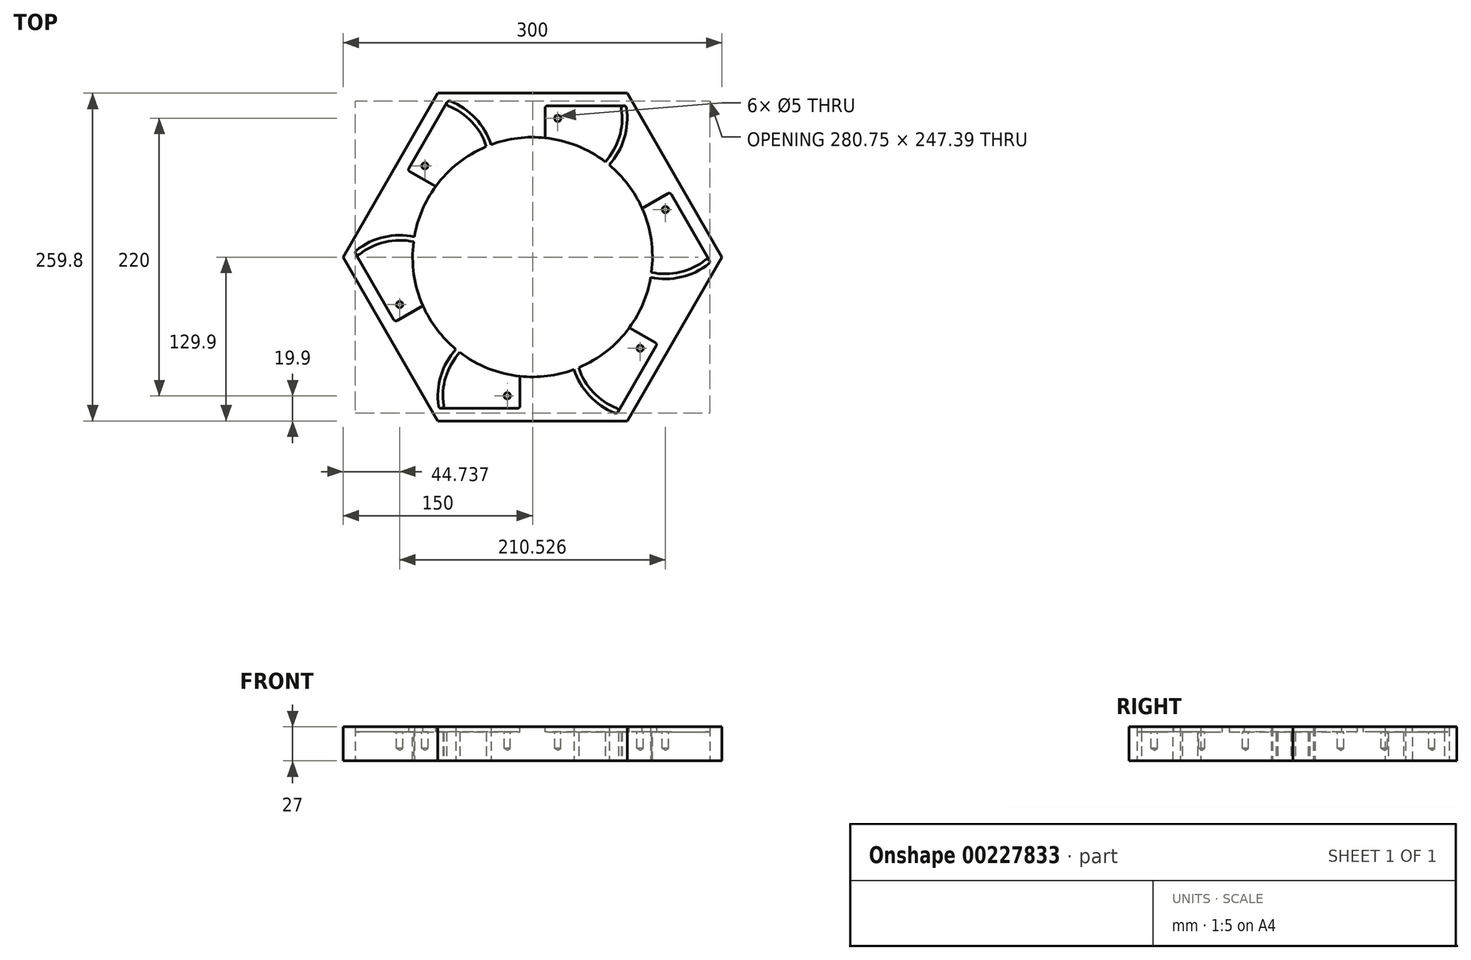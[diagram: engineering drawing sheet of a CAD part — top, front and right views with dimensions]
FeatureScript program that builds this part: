
annotation { "Feature Type Name" : "Feature", "Feature Type Description" : "" }
export const myFeature = defineFeature(function(context is Context, id is Id, definition is map)
    precondition{}
    {
        {
            var Q0;
            Q0=qCreatedBy(makeId("Top.planeOp"),FACE);
            var sketch = newSketch(context, id + "F0", { "sketchPlane" : qUnion([Q0])});
            skCircle(sketch, "E0.cCircle", {"center": v(0, 0) * mm, "radius": 150 * mm, "construction": true});
            skLineSegment(sketch, "E0.0", {"start": v(-75, 129.9) * mm, "end": v(75, 129.9) * mm});
            skLineSegment(sketch, "E0.1", {"start": v(75, 129.9) * mm, "end": v(150, 0) * mm});
            skLineSegment(sketch, "E0.2", {"start": v(150, 0) * mm, "end": v(75, -129.9) * mm});
            skLineSegment(sketch, "E0.3", {"start": v(75, -129.9) * mm, "end": v(-75, -129.9) * mm});
            skLineSegment(sketch, "E0.4", {"start": v(-75, -129.9) * mm, "end": v(-150, 0) * mm});
            skLineSegment(sketch, "E0.5", {"start": v(-150, 0) * mm, "end": v(-75, 129.9) * mm});
            skCircle(sketch, "E1", {"center": v(0, 0) * mm, "radius": 95 * mm});
            skSolve(sketch);
        }
        {
            var Q0;
            Q0 = qSketchRegion(id + "F0", true);
            extrude(context, id + "F1", {"entities" : qUnion([Q0]), "oppositeDirection" : true, "depth" : 25 * mm, "hasSecondDirection" : true, "secondDirectionOppositeDirection" : false, "secondDirectionDepth" : 2 * mm});
        }
        {
            var Q0;
            Q0=qCreatedBy(makeId("Top.planeOp"),FACE);
            var sketch = newSketch(context, id + "F2", { "sketchPlane" : qUnion([Q0])});
            skLineSegment(sketch, "E2", {"start": v(0, 0) * mm, "end": v(-115.33, 66.59) * mm, "construction": true});
            skLineSegment(sketch, "E3", {"start": v(24.73, 8.82) * mm, "end": v(-118.6, 91.57) * mm, "construction": true});
            skLineSegment(sketch, "E4", {"start": v(-73.53, 92.65) * mm, "end": v(-110.35, 28.87) * mm, "construction": true});
            skPoint(sketch, "E5", {"position": v(-85.26, 72.32) * mm});
            skArc(sketch, "E6", {"start": v(-79.2, 122.96) * mm, "mid": v(-97.67, 22.85) * mm, "end": v(-66.72, 119.83) * mm, "construction": true});
            skArc(sketch, "E7", {"start": v(-78.72, 126.93) * mm, "mid": v(-131.29, 42.21) * mm, "end": v(-32.6, 56.43) * mm});
            skCircle(sketch, "E8", {"center": v(-85.26, 72.32) * mm, "radius": 2.5 * mm, "construction": true});
            skArc(sketch, "E9", {"start": v(-86.7, 77.1) * mm, "mid": v(-89.8, 70.21) * mm, "end": v(-82.54, 68.13) * mm, "construction": true});
            skLineSegment(sketch, "E10", {"start": v(-95.36, 62.49) * mm, "end": v(-73.35, 109.7) * mm, "construction": true});
            skArc(sketch, "E11", {"start": v(-86.7, 77.1) * mm, "mid": v(-83.05, 79.12) * mm, "end": v(-80.54, 82.45) * mm, "construction": true});
            skLineSegment(sketch, "E12.trimOffspring", {"start": v(-80.54, 82.45) * mm, "end": v(-62.02, 122.17) * mm, "construction": true});
            skLineSegment(sketch, "E13.trimOffspring", {"start": v(-37.22, 89.44) * mm, "end": v(-33.46, 90.8) * mm});
            skPoint(sketch, "E14", {"position": v(-62.02, 122.17) * mm});
            skPoint(sketch, "E15", {"position": v(-33.46, 90.8) * mm});
            skArc(sketch, "E16", {"start": v(-37.22, 89.44) * mm, "mid": v(-37.91, 91.27) * mm, "end": v(-38.67, 93.07) * mm});
            skLineSegment(sketch, "E17", {"start": v(-82.54, 68.13) * mm, "end": v(-42.49, 94.14) * mm, "construction": true});
            skLineSegment(sketch, "E18", {"start": v(-50.7, 85.23) * mm, "end": v(-31.42, 97.75) * mm, "construction": true});
            skPoint(sketch, "E19", {"position": v(-39.97, 95.77) * mm});
            skCircle(sketch, "E20", {"center": v(-39.97, 95.77) * mm, "radius": 3 * mm, "construction": true});
            skPoint(sketch, "E21", {"position": v(-42.49, 94.14) * mm});
            skArc(sketch, "E22.trimOffspring", {"start": v(-39.97, 95.77) * mm, "mid": v(-49.96, 109.12) * mm, "end": v(-63.7, 118.54) * mm, "construction": true});
            skLineSegment(sketch, "E23.trimOffspring", {"start": v(-39.97, 95.77) * mm, "end": v(-16, 111.34) * mm});
            skArc(sketch, "E24", {"start": v(-38.67, 93.07) * mm, "mid": v(-40.33, 94.5) * mm, "end": v(-42.49, 94.14) * mm});
            skPoint(sketch, "E25", {"position": v(-77.2, 132.91) * mm});
            skPoint(sketch, "E26", {"position": v(-78.72, 126.93) * mm});
            skLineSegment(sketch, "E27", {"start": v(-85.26, 72.32) * mm, "end": v(-78.72, 126.93) * mm, "construction": true});
            skLineSegment(sketch, "E28", {"start": v(-85.21, 72.2) * mm, "end": v(-33.46, 90.8) * mm, "construction": true});
            skPoint(sketch, "E29", {"position": v(-56.33, 130.09) * mm});
            skLineSegment(sketch, "E30", {"start": v(-97.92, 70.4) * mm, "end": v(-67.73, 122.7) * mm});
            skLineSegment(sketch, "E31.1.0", {"start": v(0, 0) * mm, "end": v(-115.33, -66.59) * mm});
            skPoint(sketch, "E31.1.1", {"position": v(-105.26, -37.68) * mm});
            skLineSegment(sketch, "E31.2.0", {"start": v(0, 0) * mm, "end": v(0, -133.17) * mm});
            skPoint(sketch, "E31.2.1", {"position": v(-20, -110) * mm});
            skLineSegment(sketch, "E31.3.0", {"start": v(0, 0) * mm, "end": v(115.33, -66.59) * mm});
            skPoint(sketch, "E31.3.1", {"position": v(85.26, -72.32) * mm});
            skLineSegment(sketch, "E31.4.0", {"start": v(0, 0) * mm, "end": v(115.33, 66.59) * mm});
            skPoint(sketch, "E31.4.1", {"position": v(105.26, 37.68) * mm});
            skLineSegment(sketch, "E31.5.0", {"start": v(0, 0) * mm, "end": v(0, 133.17) * mm});
            skPoint(sketch, "E31.5.1", {"position": v(20, 110) * mm});
            skPoint(sketch, "E31.center", {"position": v(0, 0) * mm});
            skCircle(sketch, "E32.0", {"center": v(0, 0) * mm, "radius": 95 * mm, "construction": true});
            skPoint(sketch, "E33", {"position": v(-32.9, 89.12) * mm});
            skLineSegment(sketch, "E34", {"start": v(-32.9, 89.12) * mm, "end": v(32.9, -89.12) * mm, "construction": true});
            skPoint(sketch, "E35", {"position": v(-22.5, 60.98) * mm});
            skPoint(sketch, "E36", {"position": v(5.2, -14.07) * mm});
            skCircle(sketch, "E37", {"center": v(5.2, -14.07) * mm, "radius": 80 * mm, "construction": true});
            skArc(sketch, "E38.filletArc", {"start": v(-65.27, 123.56) * mm, "mid": v(-66.66, 123.58) * mm, "end": v(-67.73, 122.7) * mm});
            skLineSegment(sketch, "E39", {"start": v(-32.6, 56.43) * mm, "end": v(-85.26, 72.32) * mm, "construction": true});
            skLineSegment(sketch, "E40", {"start": v(-76.12, 72.3) * mm, "end": v(-85.21, 72.2) * mm});
            skLineSegment(sketch, "E41", {"start": v(-85.21, 72.2) * mm, "end": v(-56.33, 90.95) * mm, "construction": true});
            skLineSegment(sketch, "E42", {"start": v(-85.21, 72.2) * mm, "end": v(-48.78, 69.91) * mm, "construction": true});
            skLineSegment(sketch, "E43", {"start": v(-48.77, 65.04) * mm, "end": v(-92.23, 67.76) * mm, "construction": true});
            skCircle(sketch, "E44", {"center": v(-85.21, 72.2) * mm, "radius": 10 * mm, "construction": true});
            skLineSegment(sketch, "E45", {"start": v(-87.5, 62.45) * mm, "end": v(-55.32, 60.44) * mm, "construction": true});
            skLineSegment(sketch, "E46", {"start": v(-97.2, 67.66) * mm, "end": v(-68.1, 50.87) * mm});
            skArc(sketch, "E47.filletArc", {"start": v(-97.92, 70.4) * mm, "mid": v(-98.12, 68.87) * mm, "end": v(-97.2, 67.66) * mm});
            skArc(sketch, "E48", {"start": v(-67.73, 122.7) * mm, "mid": v(-67.88, 121.03) * mm, "end": v(-66.72, 119.83) * mm, "construction": true});
            skArc(sketch, "E49.converted", {"start": v(-30.7, 79.26) * mm, "mid": v(-41.9, 106.16) * mm, "end": v(-65.27, 123.56) * mm});
            skArc(sketch, "E50", {"start": v(-30.7, 79.26) * mm, "mid": v(-51.4, 67.7) * mm, "end": v(-68.1, 50.87) * mm});
            skLineSegment(sketch, "E51.trimOffspring", {"start": v(-52.18, 41.68) * mm, "end": v(-31.82, 29.92) * mm});
            skSolve(sketch);
        }
        {
            var Q0;
            Q0=qCreatedBy(makeId("Front.planeOp"),FACE);
            var sketch = newSketch(context, id + "F3", { "sketchPlane" : qUnion([Q0])});
            skLineSegment(sketch, "E52", {"start": v(0, -93.36) * mm, "end": v(0, 93) * mm, "construction": true});
            skSolve(sketch);
        }
        {
            var Q0;
            Q0 = qSketchRegion(id + "F2", true);
            extrude(context, id + "F4", {"entities" : qUnion([Q0]), "depth" : 25 * mm, "hasSecondDirection" : true, "secondDirectionOppositeDirection" : true, "secondDirectionDepth" : 2 * mm});
        }
        {
            var Q0;
            Q0=makeQuery(id+"F4.opExtrude","SWEPT_BODY",BODY,{"disambiguationData":[OSD([sQuery(id+"F2.wireOp",EDGE,"E30"),sQuery(id+"F2.wireOp",EDGE,"E38.filletArc"),sQuery(id+"F2.wireOp",EDGE,"E46"),sQuery(id+"F2.wireOp",EDGE,"E47.filletArc"),sQuery(id+"F2.wireOp",EDGE,"E50"),sQuery(id+"F2.wireOp",EDGE,"E49.converted")])]});
            var Q1;
            Q1=sQuery(id+"F3.wireOp",EDGE,"E52");
            circularPattern(context, id + "F5", {"entities" : qUnion([Q0]), "axis" : qUnion([Q1]), "angle" : 360 * degree, "instanceCount" : 6, "equalSpace" : true});
        }
        {
            var Q0;
            Q0=makeQuery(id+"F5.opPattern","COPY",BODY,{"derivedFrom":makeQuery(id+"F4.opExtrude","SWEPT_BODY",BODY,{"disambiguationData":[OSD([sQuery(id+"F2.wireOp",EDGE,"E30"),sQuery(id+"F2.wireOp",EDGE,"E38.filletArc"),sQuery(id+"F2.wireOp",EDGE,"E46"),sQuery(id+"F2.wireOp",EDGE,"E47.filletArc"),sQuery(id+"F2.wireOp",EDGE,"E50"),sQuery(id+"F2.wireOp",EDGE,"E49.converted")])]}),"instanceName":"1"});
            var Q1;
            Q1=makeQuery(id+"F4.opExtrude","SWEPT_BODY",BODY,{"disambiguationData":[OSD([sQuery(id+"F2.wireOp",EDGE,"E30"),sQuery(id+"F2.wireOp",EDGE,"E38.filletArc"),sQuery(id+"F2.wireOp",EDGE,"E46"),sQuery(id+"F2.wireOp",EDGE,"E47.filletArc"),sQuery(id+"F2.wireOp",EDGE,"E50"),sQuery(id+"F2.wireOp",EDGE,"E49.converted")])]});
            var Q2;
            Q2=makeQuery(id+"F5.opPattern","COPY",BODY,{"derivedFrom":makeQuery(id+"F4.opExtrude","SWEPT_BODY",BODY,{"disambiguationData":[OSD([sQuery(id+"F2.wireOp",EDGE,"E30"),sQuery(id+"F2.wireOp",EDGE,"E38.filletArc"),sQuery(id+"F2.wireOp",EDGE,"E46"),sQuery(id+"F2.wireOp",EDGE,"E47.filletArc"),sQuery(id+"F2.wireOp",EDGE,"E50"),sQuery(id+"F2.wireOp",EDGE,"E49.converted")])]}),"instanceName":"5"});
            var Q3;
            Q3=makeQuery(id+"F5.opPattern","COPY",BODY,{"derivedFrom":makeQuery(id+"F4.opExtrude","SWEPT_BODY",BODY,{"disambiguationData":[OSD([sQuery(id+"F2.wireOp",EDGE,"E30"),sQuery(id+"F2.wireOp",EDGE,"E38.filletArc"),sQuery(id+"F2.wireOp",EDGE,"E46"),sQuery(id+"F2.wireOp",EDGE,"E47.filletArc"),sQuery(id+"F2.wireOp",EDGE,"E50"),sQuery(id+"F2.wireOp",EDGE,"E49.converted")])]}),"instanceName":"4"});
            var Q4;
            Q4=makeQuery(id+"F5.opPattern","COPY",BODY,{"derivedFrom":makeQuery(id+"F4.opExtrude","SWEPT_BODY",BODY,{"disambiguationData":[OSD([sQuery(id+"F2.wireOp",EDGE,"E30"),sQuery(id+"F2.wireOp",EDGE,"E38.filletArc"),sQuery(id+"F2.wireOp",EDGE,"E46"),sQuery(id+"F2.wireOp",EDGE,"E47.filletArc"),sQuery(id+"F2.wireOp",EDGE,"E50"),sQuery(id+"F2.wireOp",EDGE,"E49.converted")])]}),"instanceName":"3"});
            var Q5;
            Q5=makeQuery(id+"F5.opPattern","COPY",BODY,{"derivedFrom":makeQuery(id+"F4.opExtrude","SWEPT_BODY",BODY,{"disambiguationData":[OSD([sQuery(id+"F2.wireOp",EDGE,"E30"),sQuery(id+"F2.wireOp",EDGE,"E38.filletArc"),sQuery(id+"F2.wireOp",EDGE,"E46"),sQuery(id+"F2.wireOp",EDGE,"E47.filletArc"),sQuery(id+"F2.wireOp",EDGE,"E50"),sQuery(id+"F2.wireOp",EDGE,"E49.converted")])]}),"instanceName":"2"});
            var Q6;
            Q6=makeQuery(id+"F1.opExtrude","SWEPT_BODY",BODY,{"disambiguationData":[OSD([sQuery(id+"F0.wireOp",EDGE,"E0.0"),sQuery(id+"F0.wireOp",EDGE,"E0.1"),sQuery(id+"F0.wireOp",EDGE,"E0.2"),sQuery(id+"F0.wireOp",EDGE,"E0.3"),sQuery(id+"F0.wireOp",EDGE,"E0.4"),sQuery(id+"F0.wireOp",EDGE,"E0.5"),sQuery(id+"F0.wireOp",EDGE,"E1")])]});
            booleanBodies(context, id + "F6", {"operationType" : BooleanOperationType.SUBTRACTION, "tools" : qUnion([Q0, Q1, Q2, Q3, Q4, Q5]), "targets" : qUnion([Q6])});
        }
        {
            var Q0;
            Q0=makeQuery(id+"F0.imprint","IMPRINT",FACE,{"disambiguationData":[TD([[makeQuery(id+"F0.imprint","IMPRINT",EDGE,{"derivedFrom":sQuery(id+"F0.wireOp",EDGE,"E1")}),1.0]])]});
            var sketch = newSketch(context, id + "F7", { "sketchPlane" : qUnion([Q0])});
            skArc(sketch, "E53.1", {"start": v(-34.54, 77.66) * mm, "mid": v(-44.72, 103.26) * mm, "end": v(-66.72, 119.83) * mm});
            skArc(sketch, "E54.0", {"start": v(-30.7, 79.26) * mm, "mid": v(-32.63, 78.49) * mm, "end": v(-34.54, 77.66) * mm});
            skArc(sketch, "E55.0", {"start": v(-67.73, 122.7) * mm, "mid": v(-67.88, 121.03) * mm, "end": v(-66.72, 119.83) * mm});
            skArc(sketch, "E55.1", {"start": v(-65.27, 123.56) * mm, "mid": v(-66.66, 123.58) * mm, "end": v(-67.73, 122.7) * mm});
            skArc(sketch, "E55.2", {"start": v(-30.7, 79.26) * mm, "mid": v(-41.9, 106.16) * mm, "end": v(-65.27, 123.56) * mm});
            skPoint(sketch, "E56.orphan", {"position": v(-68.1, 50.87) * mm});
            skPoint(sketch, "E57.orphan", {"position": v(-79.2, 122.96) * mm});
            skPoint(sketch, "E53.0.end.orphan", {"position": v(-97.92, 70.4) * mm});
            skPoint(sketch, "E53.0.start.orphan", {"position": v(-67.73, 122.7) * mm});
            skSolve(sketch);
        }
        {
            var Q0;
            Q0 = qSketchRegion(id + "F7", true);
            extrude(context, id + "F8", {"entities" : qUnion([Q0]), "depth" : 10 * mm, "hasSecondDirection" : true, "secondDirectionOppositeDirection" : true, "secondDirectionDepth" : 35 * mm});
        }
        {
            var Q0;
            Q0=makeQuery(id+"F8.opExtrude","SWEPT_BODY",BODY,{"disambiguationData":[OSD([sQuery(id+"F7.wireOp",EDGE,"E53.1"),sQuery(id+"F7.wireOp",EDGE,"E54.0"),sQuery(id+"F7.wireOp",EDGE,"E55.0"),sQuery(id+"F7.wireOp",EDGE,"E55.1"),sQuery(id+"F7.wireOp",EDGE,"E55.2")])]});
            var Q1;
            Q1=sQuery(id+"F3.wireOp",EDGE,"E52");
            circularPattern(context, id + "F9", {"entities" : qUnion([Q0]), "axis" : qUnion([Q1]), "angle" : 360 * degree, "instanceCount" : 6, "equalSpace" : true});
        }
        {
            var Q0;
            Q0=makeQuery(id+"F8.opExtrude","SWEPT_BODY",BODY,{"disambiguationData":[OSD([sQuery(id+"F7.wireOp",EDGE,"E53.1"),sQuery(id+"F7.wireOp",EDGE,"E54.0"),sQuery(id+"F7.wireOp",EDGE,"E55.0"),sQuery(id+"F7.wireOp",EDGE,"E55.1"),sQuery(id+"F7.wireOp",EDGE,"E55.2")])]});
            var Q1;
            Q1=makeQuery(id+"F9.opPattern","COPY",BODY,{"derivedFrom":makeQuery(id+"F8.opExtrude","SWEPT_BODY",BODY,{"disambiguationData":[OSD([sQuery(id+"F7.wireOp",EDGE,"E53.1"),sQuery(id+"F7.wireOp",EDGE,"E54.0"),sQuery(id+"F7.wireOp",EDGE,"E55.0"),sQuery(id+"F7.wireOp",EDGE,"E55.1"),sQuery(id+"F7.wireOp",EDGE,"E55.2")])]}),"instanceName":"5"});
            var Q2;
            Q2=makeQuery(id+"F9.opPattern","COPY",BODY,{"derivedFrom":makeQuery(id+"F8.opExtrude","SWEPT_BODY",BODY,{"disambiguationData":[OSD([sQuery(id+"F7.wireOp",EDGE,"E53.1"),sQuery(id+"F7.wireOp",EDGE,"E54.0"),sQuery(id+"F7.wireOp",EDGE,"E55.0"),sQuery(id+"F7.wireOp",EDGE,"E55.1"),sQuery(id+"F7.wireOp",EDGE,"E55.2")])]}),"instanceName":"4"});
            var Q3;
            Q3=makeQuery(id+"F9.opPattern","COPY",BODY,{"derivedFrom":makeQuery(id+"F8.opExtrude","SWEPT_BODY",BODY,{"disambiguationData":[OSD([sQuery(id+"F7.wireOp",EDGE,"E53.1"),sQuery(id+"F7.wireOp",EDGE,"E54.0"),sQuery(id+"F7.wireOp",EDGE,"E55.0"),sQuery(id+"F7.wireOp",EDGE,"E55.1"),sQuery(id+"F7.wireOp",EDGE,"E55.2")])]}),"instanceName":"3"});
            var Q4;
            Q4=makeQuery(id+"F9.opPattern","COPY",BODY,{"derivedFrom":makeQuery(id+"F8.opExtrude","SWEPT_BODY",BODY,{"disambiguationData":[OSD([sQuery(id+"F7.wireOp",EDGE,"E53.1"),sQuery(id+"F7.wireOp",EDGE,"E54.0"),sQuery(id+"F7.wireOp",EDGE,"E55.0"),sQuery(id+"F7.wireOp",EDGE,"E55.1"),sQuery(id+"F7.wireOp",EDGE,"E55.2")])]}),"instanceName":"2"});
            var Q5;
            Q5=makeQuery(id+"F9.opPattern","COPY",BODY,{"derivedFrom":makeQuery(id+"F8.opExtrude","SWEPT_BODY",BODY,{"disambiguationData":[OSD([sQuery(id+"F7.wireOp",EDGE,"E53.1"),sQuery(id+"F7.wireOp",EDGE,"E54.0"),sQuery(id+"F7.wireOp",EDGE,"E55.0"),sQuery(id+"F7.wireOp",EDGE,"E55.1"),sQuery(id+"F7.wireOp",EDGE,"E55.2")])]}),"instanceName":"1"});
            var Q6;
            Q6=makeQuery(id+"F1.opExtrude","SWEPT_BODY",BODY,{"disambiguationData":[OSD([sQuery(id+"F0.wireOp",EDGE,"E0.0"),sQuery(id+"F0.wireOp",EDGE,"E0.1"),sQuery(id+"F0.wireOp",EDGE,"E0.2"),sQuery(id+"F0.wireOp",EDGE,"E0.3"),sQuery(id+"F0.wireOp",EDGE,"E0.4"),sQuery(id+"F0.wireOp",EDGE,"E0.5"),sQuery(id+"F0.wireOp",EDGE,"E1")])]});
            booleanBodies(context, id + "F10", {"operationType" : BooleanOperationType.SUBTRACTION, "tools" : qUnion([Q0, Q1, Q2, Q3, Q4, Q5]), "targets" : qUnion([Q6])});
        }
        {
            var Q0;
            Q0=sQuery(id+"F2.wireOp",VERTEX,"E31.5.1");
            var Q1;
            Q1=sQuery(id+"F2.wireOp",VERTEX,"E31.4.1");
            var Q2;
            Q2=sQuery(id+"F2.wireOp",VERTEX,"E31.3.1");
            var Q3;
            Q3=sQuery(id+"F2.wireOp",VERTEX,"E31.2.1");
            var Q4;
            Q4=sQuery(id+"F2.wireOp",VERTEX,"E31.1.1");
            var Q5;
            Q5=sQuery(id+"F2.wireOp",VERTEX,"E5");
            var Q6;
            Q6=makeQuery(id+"F1.opExtrude","SWEPT_BODY",BODY,{"disambiguationData":[OSD([sQuery(id+"F0.wireOp",EDGE,"E0.0"),sQuery(id+"F0.wireOp",EDGE,"E0.1"),sQuery(id+"F0.wireOp",EDGE,"E0.2"),sQuery(id+"F0.wireOp",EDGE,"E0.3"),sQuery(id+"F0.wireOp",EDGE,"E0.4"),sQuery(id+"F0.wireOp",EDGE,"E0.5"),sQuery(id+"F0.wireOp",EDGE,"E1")])]});
            hole(context, id + "F11", {"style" : HoleStyle.SIMPLE, "endStyle" : HoleEndStyle.BLIND, "holeDiameter" : 5 * mm, "holeDepth" : 13 * mm, "locations" : qUnion([Q0, Q1, Q2, Q3, Q4, Q5]), "scope" : qUnion([Q6])});
        }
    });
